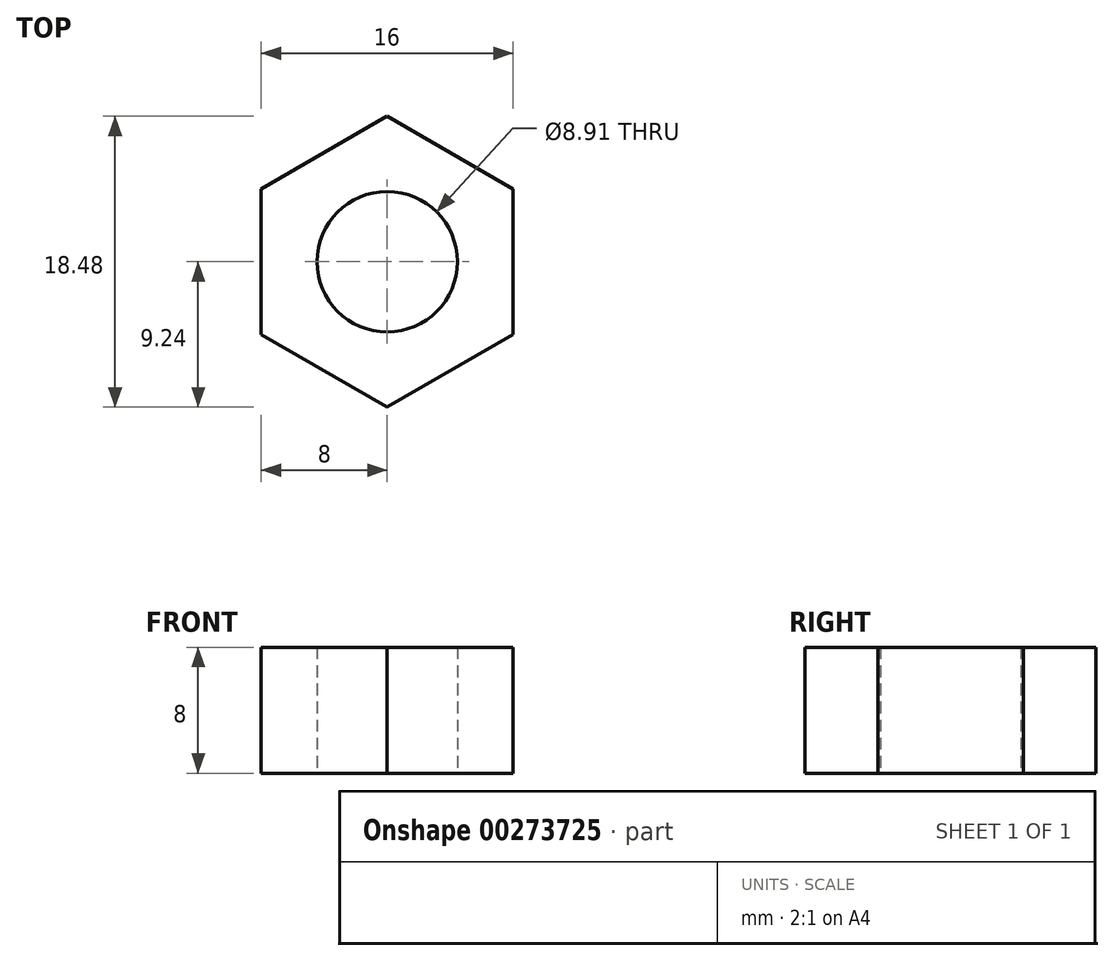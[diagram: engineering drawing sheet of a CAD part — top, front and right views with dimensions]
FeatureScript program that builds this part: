
annotation { "Feature Type Name" : "Feature", "Feature Type Description" : "" }
export const myFeature = defineFeature(function(context is Context, id is Id, definition is map)
    precondition{}
    {
        {
            var Q0;
            Q0=qCreatedBy(makeId("Top.planeOp"),FACE);
            var sketch = newSketch(context, id + "F0", { "sketchPlane" : qUnion([Q0])});
            skCircle(sketch, "E0.cCircle", {"center": v(0, 0) * mm, "radius": 8 * mm, "construction": true});
            skLineSegment(sketch, "E0.0", {"start": v(-8, -4.62) * mm, "end": v(-8, 4.62) * mm});
            skLineSegment(sketch, "E0.1", {"start": v(-8, 4.62) * mm, "end": v(0, 9.24) * mm});
            skLineSegment(sketch, "E0.2", {"start": v(0, 9.24) * mm, "end": v(8, 4.62) * mm});
            skLineSegment(sketch, "E0.3", {"start": v(8, 4.62) * mm, "end": v(8, -4.62) * mm});
            skLineSegment(sketch, "E0.4", {"start": v(8, -4.62) * mm, "end": v(0, -9.24) * mm});
            skLineSegment(sketch, "E0.5", {"start": v(0, -9.24) * mm, "end": v(-8, -4.62) * mm});
            skPoint(sketch, "E0.0.midPoint", {"position": v(-8, 0) * mm});
            skCircle(sketch, "E1", {"center": v(0, 0) * mm, "radius": 4.46 * mm});
            skSolve(sketch);
        }
        {
            var Q0;
            Q0=makeQuery(id+"F0.imprint","IMPRINT",FACE,{"disambiguationData":[TD([[makeQuery(id+"F0.imprint","IMPRINT",EDGE,{"derivedFrom":sQuery(id+"F0.wireOp",EDGE,"E0.0")}),-1.0]])]});
            extrude(context, id + "F1", {"entities" : qUnion([Q0]), "depth" : 8 * mm});
        }
    });
